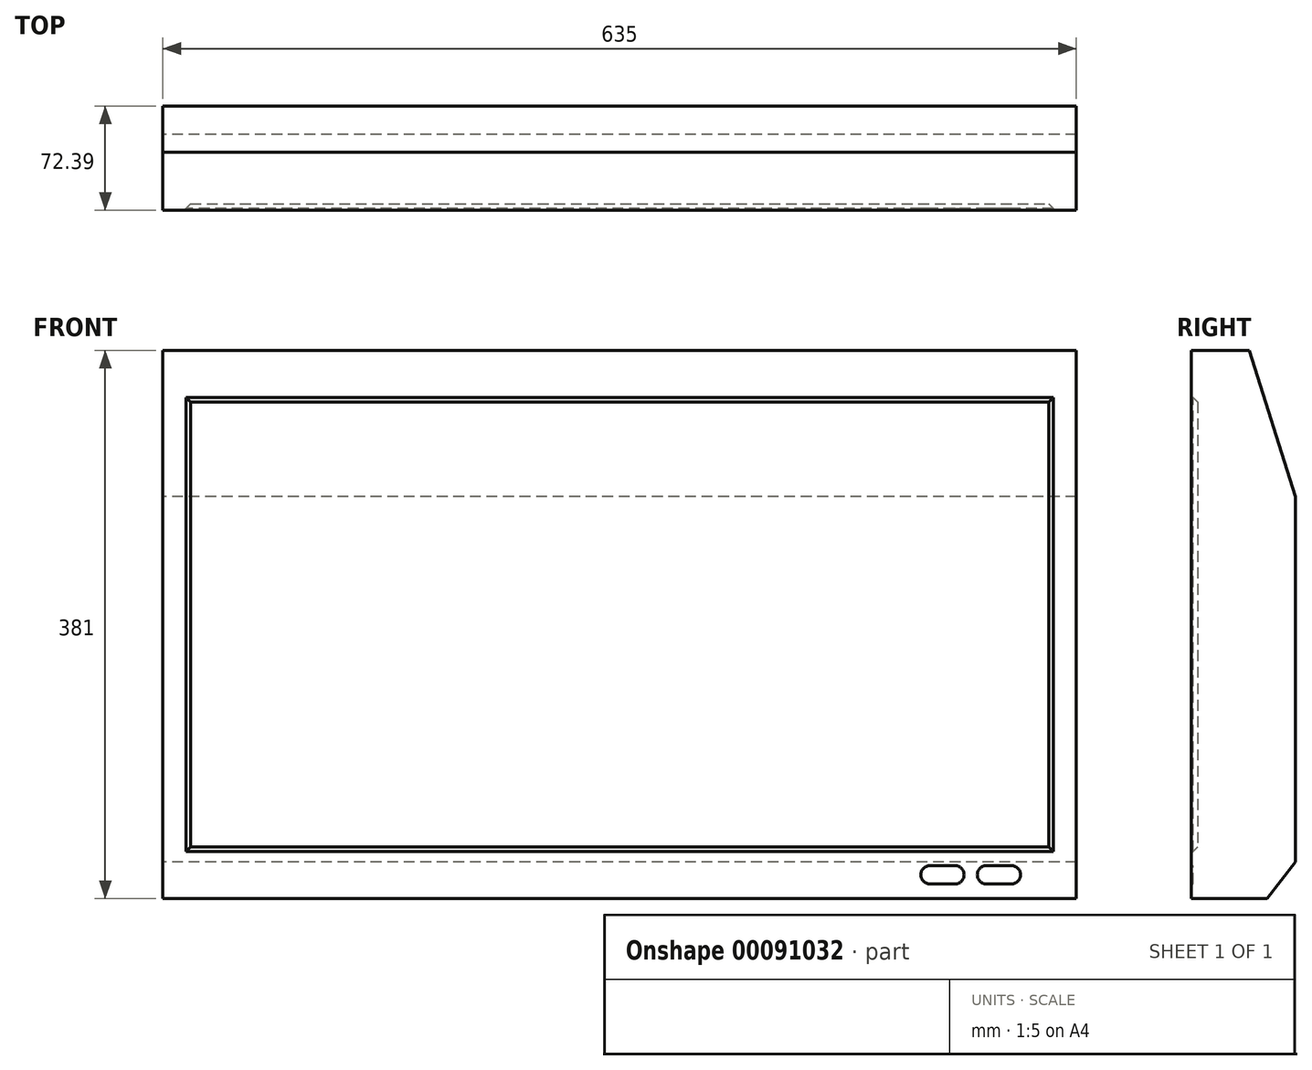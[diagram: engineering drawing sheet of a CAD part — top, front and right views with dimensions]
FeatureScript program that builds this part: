
annotation { "Feature Type Name" : "Feature", "Feature Type Description" : "" }
export const myFeature = defineFeature(function(context is Context, id is Id, definition is map)
    precondition{}
    {
        {
            var Q0;
            Q0=qCreatedBy(makeId("Right.planeOp"),FACE);
            var sketch = newSketch(context, id + "F0", { "sketchPlane" : qUnion([Q0])});
            skLineSegment(sketch, "E0", {"start": v(0, 0) * mm, "end": v(0, 381) * mm});
            skLineSegment(sketch, "E1", {"start": v(0, 381) * mm, "end": v(39.12, 381) * mm});
            skLineSegment(sketch, "E2", {"start": v(39.12, 381) * mm, "end": v(71.12, 279.4) * mm});
            skLineSegment(sketch, "E3", {"start": v(71.12, 279.4) * mm, "end": v(71.12, 25.4) * mm});
            skLineSegment(sketch, "E4", {"start": v(71.12, 25.4) * mm, "end": v(51.43, 0) * mm});
            skLineSegment(sketch, "E5", {"start": v(51.43, 0) * mm, "end": v(0, 0) * mm});
            skSolve(sketch);
        }
        {
            var Q0;
            Q0=makeQuery(id+"F0.imprint","IMPRINT",FACE,{"disambiguationData":[TD([[makeQuery(id+"F0.imprint","IMPRINT",EDGE,{"derivedFrom":sQuery(id+"F0.wireOp",EDGE,"E0")}),-1.0]])]});
            extrude(context, id + "F1", {"entities" : qUnion([Q0]), "endBound" : BoundingType.SYMMETRIC, "depth" : 635 * mm});
        }
        {
            var Q0;
            Q0=makeQuery(id+"F1.opExtrude","SWEPT_FACE",FACE,{"disambiguationData":[OSD([sQuery(id+"F0.wireOp",EDGE,"E0")])]});
            var sketch = newSketch(context, id + "F2", { "sketchPlane" : qUnion([Q0])});
            skLineSegment(sketch, "E6.bottom", {"start": v(-303.43, 350.21) * mm, "end": v(303.43, 350.21) * mm});
            skLineSegment(sketch, "E6.top", {"start": v(-303.43, 30.79) * mm, "end": v(303.43, 30.79) * mm});
            skLineSegment(sketch, "E6.left", {"start": v(-303.43, 350.21) * mm, "end": v(-303.43, 30.79) * mm});
            skLineSegment(sketch, "E6.right", {"start": v(303.43, 350.21) * mm, "end": v(303.43, 30.79) * mm});
            skLineSegment(sketch, "E7", {"start": v(-303.43, 350.21) * mm, "end": v(303.43, 30.79) * mm, "construction": true});
            skLineSegment(sketch, "E8", {"start": v(-303.43, 350.21) * mm, "end": v(-317.5, 350.21) * mm, "construction": true});
            skLineSegment(sketch, "E9", {"start": v(-303.43, 350.21) * mm, "end": v(-303.43, 381) * mm, "construction": true});
            skLineSegment(sketch, "E10", {"start": v(303.43, 30.79) * mm, "end": v(303.43, 0) * mm, "construction": true});
            skLineSegment(sketch, "E11", {"start": v(303.43, 30.79) * mm, "end": v(317.5, 30.79) * mm, "construction": true});
            skSolve(sketch);
        }
        {
            var Q0;
            Q0=makeQuery(id+"F2.imprint","IMPRINT",FACE,{"disambiguationData":[TD([[makeQuery(id+"F2.imprint","IMPRINT",EDGE,{"derivedFrom":sQuery(id+"F2.wireOp",EDGE,"E6.bottom")}),-1.0]])]});
            extrude(context, id + "F3", {"entities" : qUnion([Q0]), "operationType" : NewBodyOperationType.REMOVE, "oppositeDirection" : true, "depth" : 3.17 * mm});
        }
        {
            var Q0;
            Q0=makeQuery(id+"F3.boolean.opBoolean","COPY",EDGE,{"derivedFrom":makeQuery(id+"F3.opExtrude","CAP_EDGE",EDGE,{"disambiguationData":[OSD([sQuery(id+"F2.wireOp",EDGE,"E6.left")])],"isStart":false})});
            var Q1;
            Q1=makeQuery(id+"F3.boolean.opBoolean","COPY",EDGE,{"derivedFrom":makeQuery(id+"F3.opExtrude","CAP_EDGE",EDGE,{"disambiguationData":[OSD([sQuery(id+"F2.wireOp",EDGE,"E6.bottom")])],"isStart":false})});
            var Q2;
            Q2=makeQuery(id+"F3.boolean.opBoolean","COPY",EDGE,{"derivedFrom":makeQuery(id+"F3.opExtrude","CAP_EDGE",EDGE,{"disambiguationData":[OSD([sQuery(id+"F2.wireOp",EDGE,"E6.right")])],"isStart":false})});
            var Q3;
            Q3=makeQuery(id+"F3.boolean.opBoolean","COPY",EDGE,{"derivedFrom":makeQuery(id+"F3.opExtrude","CAP_EDGE",EDGE,{"disambiguationData":[OSD([sQuery(id+"F2.wireOp",EDGE,"E6.top")])],"isStart":false})});
            chamfer(context, id + "F4", {"entities" : qUnion([Q0, Q1, Q2, Q3]), "width" : 5.08 * mm, "tangentPropagation" : true});
        }
        {
            var Q0;
            Q0=makeQuery(id+"F1.opExtrude","SWEPT_FACE",FACE,{"disambiguationData":[OSD([sQuery(id+"F0.wireOp",EDGE,"E0")])]});
            var sketch = newSketch(context, id + "F5", { "sketchPlane" : qUnion([Q0])});
            skCircle(sketch, "E12", {"center": v(289.3, 16.54) * mm, "radius": 4.23 * mm});
            skLineSegment(sketch, "E13", {"start": v(272.4, 16.54) * mm, "end": v(255, 16.54) * mm});
            skLineSegment(sketch, "E14", {"start": v(233.15, 16.54) * mm, "end": v(215.76, 16.54) * mm});
            skArc(sketch, "E15.0.startCap", {"start": v(272.4, 22.9) * mm, "mid": v(278.75, 16.54) * mm, "end": v(272.4, 10.2) * mm});
            skArc(sketch, "E15.0.endCap", {"start": v(255, 10.2) * mm, "mid": v(248.66, 16.54) * mm, "end": v(255, 22.9) * mm});
            skLineSegment(sketch, "E15.0.left", {"start": v(272.4, 10.2) * mm, "end": v(255, 10.2) * mm});
            skLineSegment(sketch, "E15.0.right", {"start": v(272.4, 22.9) * mm, "end": v(255, 22.9) * mm});
            skArc(sketch, "E16.0.startCap", {"start": v(233.15, 22.9) * mm, "mid": v(239.5, 16.54) * mm, "end": v(233.15, 10.2) * mm});
            skArc(sketch, "E16.0.endCap", {"start": v(215.76, 10.2) * mm, "mid": v(209.4, 16.54) * mm, "end": v(215.76, 22.9) * mm});
            skLineSegment(sketch, "E16.0.left", {"start": v(233.15, 10.2) * mm, "end": v(215.76, 10.2) * mm});
            skLineSegment(sketch, "E16.0.right", {"start": v(233.15, 22.9) * mm, "end": v(215.76, 22.9) * mm});
            skSolve(sketch);
        }
        {
            var Q0;
            Q0=makeQuery(id+"F5.imprint","IMPRINT",FACE,{"disambiguationData":[TD([[makeQuery(id+"F5.imprint","IMPRINT",EDGE,{"derivedFrom":sQuery(id+"F5.wireOp",EDGE,"E16.0.startCap")}),-1.0]])]});
            var Q1;
            Q1=makeQuery(id+"F5.imprint","IMPRINT",FACE,{"disambiguationData":[TD([[makeQuery(id+"F5.imprint","IMPRINT",EDGE,{"derivedFrom":sQuery(id+"F5.wireOp",EDGE,"E15.0.startCap")}),-1.0]])]});
            var Q2;
            Q2=makeQuery(id+"F5.imprint","IMPRINT",FACE,{"disambiguationData":[TD([[makeQuery(id+"F5.imprint","IMPRINT",EDGE,{"derivedFrom":sQuery(id+"F5.wireOp",EDGE,"E12")}),1.0]])]});
            extrude(context, id + "F6", {"entities" : qUnion([Q0, Q1, Q2]), "operationType" : NewBodyOperationType.ADD, "depth" : 1.27 * mm});
        }
    });
